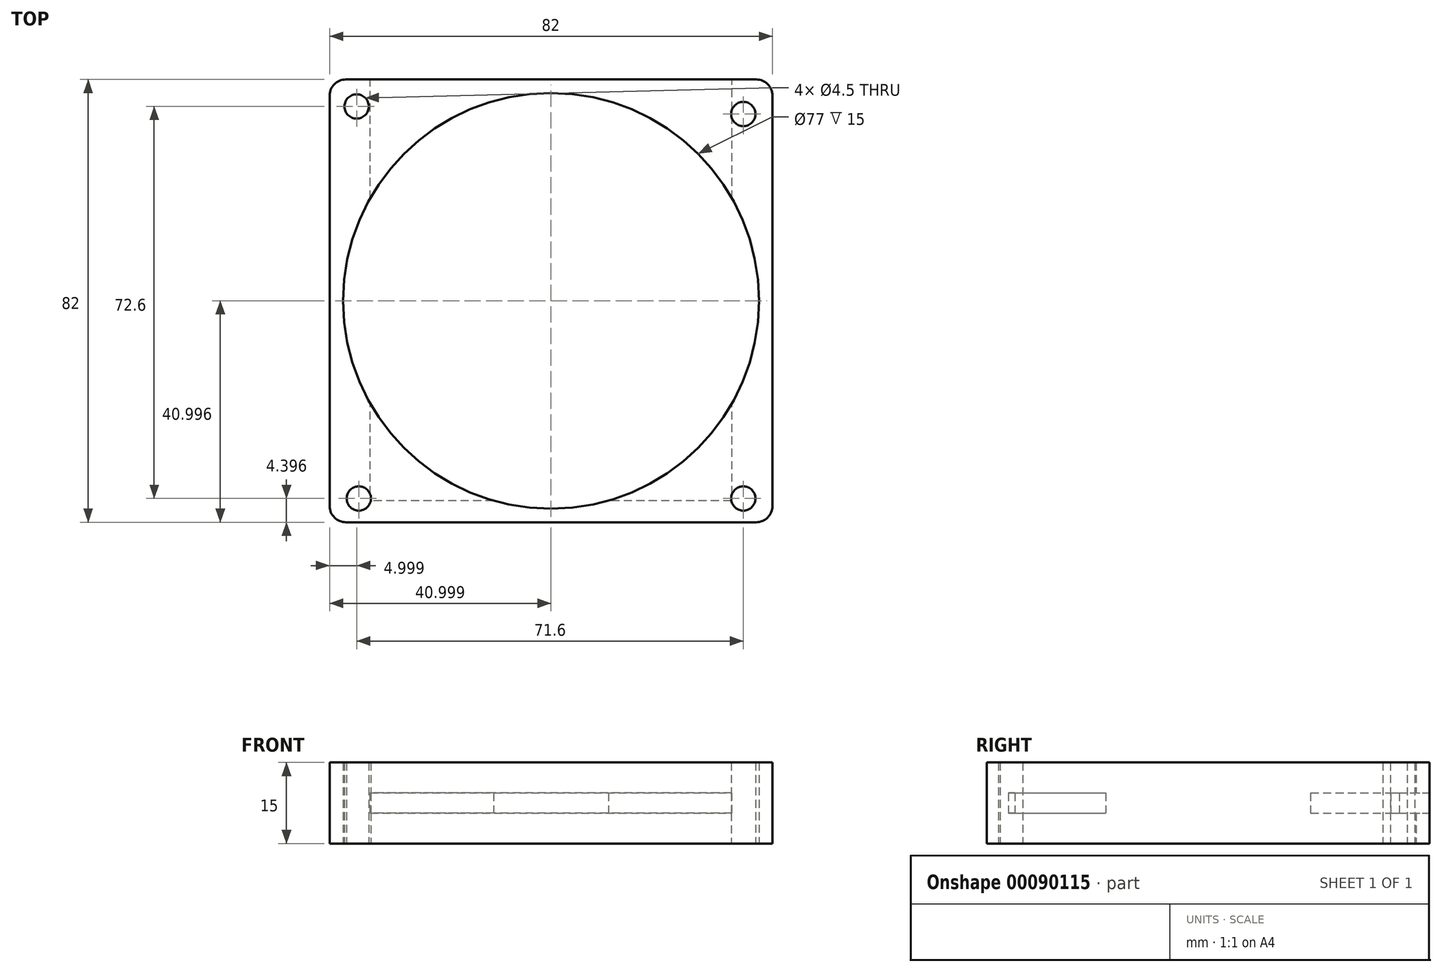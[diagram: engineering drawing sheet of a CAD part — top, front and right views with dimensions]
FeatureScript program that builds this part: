
annotation { "Feature Type Name" : "Feature", "Feature Type Description" : "" }
export const myFeature = defineFeature(function(context is Context, id is Id, definition is map)
    precondition{}
    {
        {
            var Q0;
            Q0=qCreatedBy(makeId("Top.planeOp"),FACE);
            var sketch = newSketch(context, id + "F0", { "sketchPlane" : qUnion([Q0])});
            skLineSegment(sketch, "E0.bottom", {"start": v(-25.66, -8.97) * mm, "end": v(-101.66, -8.97) * mm});
            skLineSegment(sketch, "E0.top", {"start": v(-25.66, -90.97) * mm, "end": v(-101.66, -90.97) * mm});
            skLineSegment(sketch, "E0.left", {"start": v(-22.66, -11.97) * mm, "end": v(-22.66, -87.97) * mm});
            skLineSegment(sketch, "E0.right", {"start": v(-104.66, -11.97) * mm, "end": v(-104.66, -87.97) * mm});
            skPoint(sketch, "E0.middle", {"position": v(-63.66, -49.97) * mm});
            skLineSegment(sketch, "E1.bottom", {"start": v(-27.66, -13.97) * mm, "end": v(-99.66, -13.97) * mm, "construction": true});
            skLineSegment(sketch, "E1.top", {"start": v(-27.66, -85.97) * mm, "end": v(-99.66, -85.97) * mm, "construction": true});
            skLineSegment(sketch, "E1.left", {"start": v(-27.66, -13.97) * mm, "end": v(-27.66, -85.97) * mm, "construction": true});
            skLineSegment(sketch, "E1.right", {"start": v(-99.66, -13.97) * mm, "end": v(-99.66, -85.97) * mm, "construction": true});
            skCircle(sketch, "E2", {"center": v(-99.66, -13.97) * mm, "radius": 2.25 * mm});
            skCircle(sketch, "E3.MirrorC", {"center": v(-99.26, -86.57) * mm, "radius": 2.25 * mm});
            skCircle(sketch, "E4.MirrorC", {"center": v(-28.06, -15.37) * mm, "radius": 2.25 * mm});
            skCircle(sketch, "E5.MirrorC", {"center": v(-28.06, -86.57) * mm, "radius": 2.25 * mm});
            skPoint(sketch, "E6.visualSharp", {"position": v(-104.66, -8.97) * mm});
            skArc(sketch, "E6.filletArc", {"start": v(-101.66, -8.97) * mm, "mid": v(-103.78, -9.85) * mm, "end": v(-104.66, -11.97) * mm});
            skPoint(sketch, "E7.visualSharp", {"position": v(-104.66, -90.97) * mm});
            skArc(sketch, "E7.filletArc", {"start": v(-104.66, -87.97) * mm, "mid": v(-103.78, -90.1) * mm, "end": v(-101.66, -90.97) * mm});
            skPoint(sketch, "E8.visualSharp", {"position": v(-22.66, -90.97) * mm});
            skArc(sketch, "E8.filletArc", {"start": v(-25.66, -90.97) * mm, "mid": v(-23.54, -90.1) * mm, "end": v(-22.66, -87.97) * mm});
            skPoint(sketch, "E9.visualSharp", {"position": v(-22.66, -8.97) * mm});
            skArc(sketch, "E9.filletArc", {"start": v(-22.66, -11.97) * mm, "mid": v(-23.54, -9.85) * mm, "end": v(-25.66, -8.97) * mm});
            skCircle(sketch, "E10", {"center": v(-63.66, -49.97) * mm, "radius": 38.5 * mm});
            skCircle(sketch, "E11", {"center": v(-63.66, -49.97) * mm, "radius": 38.45 * mm});
            skSolve(sketch);
        }
        {
            var Q0;
            Q0=makeQuery(id+"F0.imprint","IMPRINT",FACE,{"disambiguationData":[TD([[makeQuery(id+"F0.imprint","IMPRINT",EDGE,{"derivedFrom":sQuery(id+"F0.wireOp",EDGE,"E0.bottom")}),1.0]])]});
            extrude(context, id + "F1", {"entities" : qUnion([Q0]), "depth" : 15 * mm});
        }
        {
            var Q0;
            Q0=makeQuery(id+"F1.opExtrude","SWEPT_FACE",FACE,{"disambiguationData":[OSD([sQuery(id+"F0.wireOp",EDGE,"E0.bottom")])]});
            var sketch = newSketch(context, id + "F2", { "sketchPlane" : qUnion([Q0])});
            skLineSegment(sketch, "E12.bottom", {"start": v(30.16, 5.65) * mm, "end": v(97.16, 5.65) * mm});
            skLineSegment(sketch, "E12.top", {"start": v(30.16, 9.35) * mm, "end": v(97.16, 9.35) * mm});
            skLineSegment(sketch, "E12.left", {"start": v(30.16, 5.65) * mm, "end": v(30.16, 9.35) * mm});
            skLineSegment(sketch, "E12.right", {"start": v(97.16, 5.65) * mm, "end": v(97.16, 9.35) * mm});
            skPoint(sketch, "E12.middle", {"position": v(63.66, 7.5) * mm});
            skPoint(sketch, "E12.middle.positionSnap0", {"position": v(25.66, 7.5) * mm});
            skPoint(sketch, "E12.middle.positionSnap1", {"position": v(63.66, 15) * mm});
            skPoint(sketch, "E12.centerSnap0", {"position": v(25.66, 7.5) * mm});
            skPoint(sketch, "E12.centerSnap1", {"position": v(63.66, 15) * mm});
            skSolve(sketch);
        }
        {
            var Q0;
            Q0=makeQuery(id+"F2.imprint","IMPRINT",FACE,{"disambiguationData":[TD([[makeQuery(id+"F2.imprint","IMPRINT",EDGE,{"derivedFrom":sQuery(id+"F2.wireOp",EDGE,"E12.bottom")}),1.0]])]});
            extrude(context, id + "F3", {"entities" : qUnion([Q0]), "operationType" : NewBodyOperationType.REMOVE, "oppositeDirection" : true, "depth" : 78 * mm});
        }
    });
